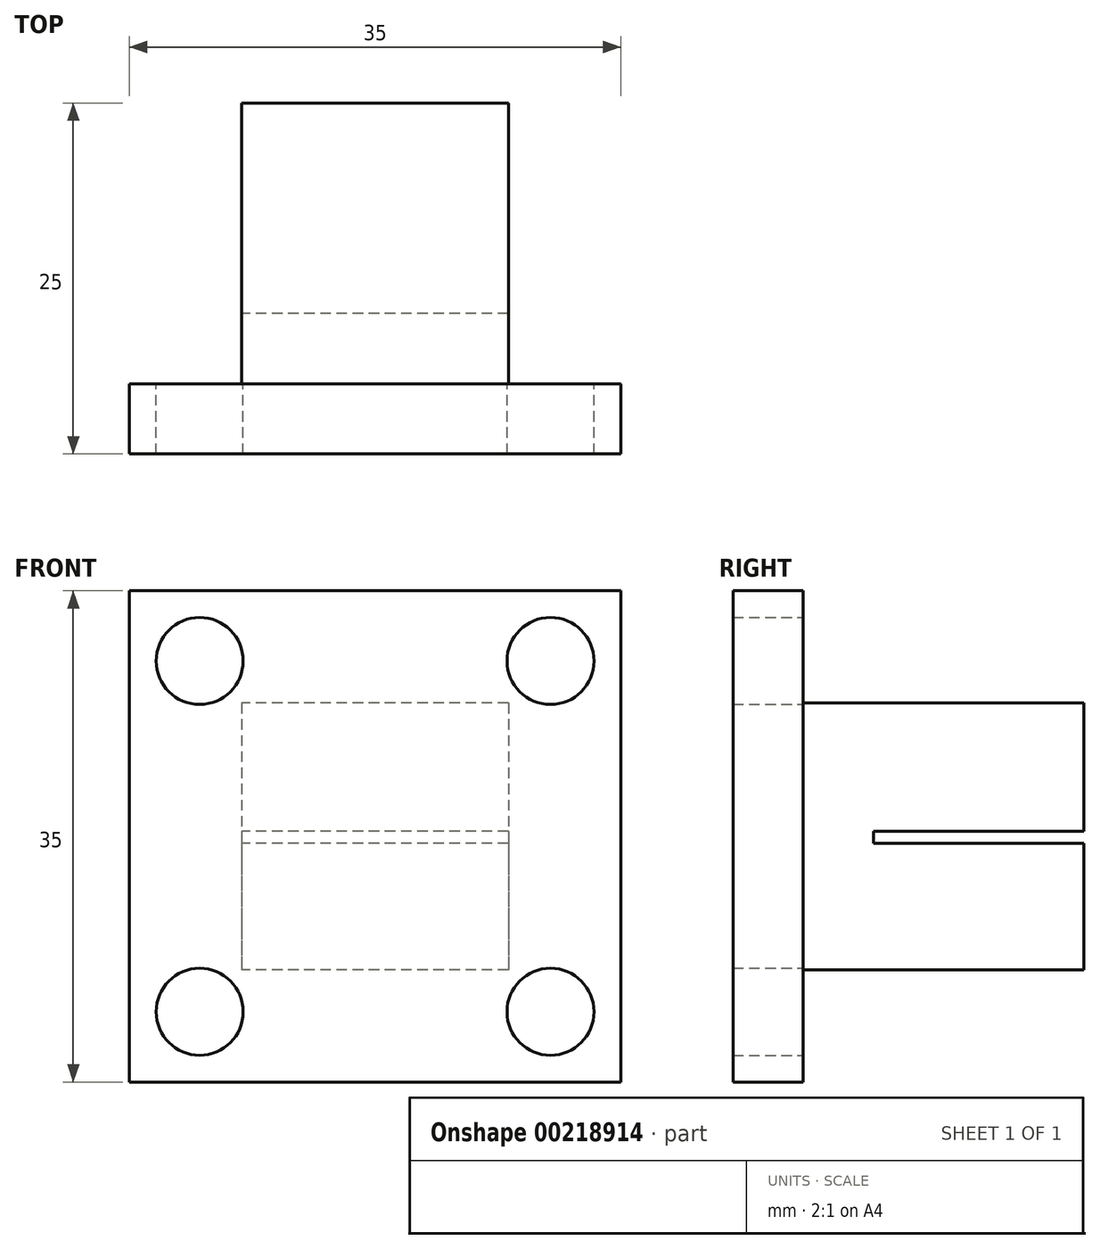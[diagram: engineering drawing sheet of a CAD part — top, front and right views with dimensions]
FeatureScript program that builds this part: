
annotation { "Feature Type Name" : "Feature", "Feature Type Description" : "" }
export const myFeature = defineFeature(function(context is Context, id is Id, definition is map)
    precondition{}
    {
        {
            var Q0;
            Q0=qCreatedBy(makeId("Front.planeOp"),FACE);
            var sketch = newSketch(context, id + "F0", { "sketchPlane" : qUnion([Q0])});
            skLineSegment(sketch, "E0.bottom", {"start": v(-16.94, 0) * mm, "end": v(18.06, 0) * mm});
            skLineSegment(sketch, "E0.top", {"start": v(-16.94, -35) * mm, "end": v(18.06, -35) * mm});
            skLineSegment(sketch, "E0.left", {"start": v(-16.94, 0) * mm, "end": v(-16.94, -35) * mm});
            skLineSegment(sketch, "E0.right", {"start": v(18.06, 0) * mm, "end": v(18.06, -35) * mm});
            skSolve(sketch);
        }
        {
            var Q0;
            Q0 = qSketchRegion(id + "F0", true);
            extrude(context, id + "F1", {"entities" : qUnion([Q0]), "depth" : 5 * mm});
        }
        {
            var Q0;
            Q0=makeQuery(id+"F1.opExtrude","CAP_FACE",FACE,{"disambiguationData":[OSD([sQuery(id+"F0.wireOp",EDGE,"E0.bottom"),sQuery(id+"F0.wireOp",EDGE,"E0.top"),sQuery(id+"F0.wireOp",EDGE,"E0.left"),sQuery(id+"F0.wireOp",EDGE,"E0.right")])],"isStart":true});
            var sketch = newSketch(context, id + "F2", { "sketchPlane" : qUnion([Q0])});
            skCircle(sketch, "E1", {"center": v(-13.06, -5) * mm, "radius": 3.1 * mm});
            skLineSegment(sketch, "E2", {"start": v(-18.06, -17.5) * mm, "end": v(16.94, -17.5) * mm});
            skCircle(sketch, "E3", {"center": v(11.94, -5) * mm, "radius": 3.1 * mm});
            skLineSegment(sketch, "E4", {"start": v(-0.56, -35) * mm, "end": v(-0.56, 0) * mm});
            skCircle(sketch, "E5", {"center": v(-13.06, -30) * mm, "radius": 3.1 * mm});
            skCircle(sketch, "E6", {"center": v(11.94, -30) * mm, "radius": 3.1 * mm});
            skSolve(sketch);
        }
        {
            var Q0;
            Q0 = qSketchRegion(id + "F2", true);
            extrude(context, id + "F3", {"entities" : qUnion([Q0]), "operationType" : NewBodyOperationType.REMOVE, "endBound" : BoundingType.THROUGH_ALL, "oppositeDirection" : true, "depth" : 25 * mm});
        }
        {
            var Q0;
            Q0=makeQuery(id+"F1.opExtrude","CAP_FACE",FACE,{"disambiguationData":[OSD([sQuery(id+"F0.wireOp",EDGE,"E0.bottom"),sQuery(id+"F0.wireOp",EDGE,"E0.top"),sQuery(id+"F0.wireOp",EDGE,"E0.left"),sQuery(id+"F0.wireOp",EDGE,"E0.right")])],"isStart":true});
            var sketch = newSketch(context, id + "F4", { "sketchPlane" : qUnion([Q0])});
            skLineSegment(sketch, "E7.bottom", {"start": v(-10.06, -8) * mm, "end": v(8.94, -8) * mm});
            skLineSegment(sketch, "E7.top", {"start": v(-10.06, -27) * mm, "end": v(8.94, -27) * mm});
            skLineSegment(sketch, "E7.left", {"start": v(-10.06, -8) * mm, "end": v(-10.06, -27) * mm});
            skLineSegment(sketch, "E7.right", {"start": v(8.94, -8) * mm, "end": v(8.94, -27) * mm});
            skSolve(sketch);
        }
        {
            var Q0;
            Q0=makeQuery(id+"F4.imprint","IMPRINT",FACE,{"disambiguationData":[TD([[makeQuery(id+"F4.imprint","IMPRINT",EDGE,{"derivedFrom":sQuery(id+"F4.wireOp",EDGE,"E7.bottom")}),-1.0]])]});
            extrude(context, id + "F5", {"entities" : qUnion([Q0]), "operationType" : NewBodyOperationType.ADD, "depth" : 20 * mm});
        }
        {
            var Q0;
            Q0=makeQuery(id+"F5.opExtrude","CAP_FACE",FACE,{"disambiguationData":[OSD([sQuery(id+"F4.wireOp",EDGE,"E7.bottom"),sQuery(id+"F4.wireOp",EDGE,"E7.top"),sQuery(id+"F4.wireOp",EDGE,"E7.left"),sQuery(id+"F4.wireOp",EDGE,"E7.right")])],"isStart":false});
            var sketch = newSketch(context, id + "F6", { "sketchPlane" : qUnion([Q0])});
            skLineSegment(sketch, "E8.bottom", {"start": v(-10.06, -17.15) * mm, "end": v(8.94, -17.15) * mm});
            skLineSegment(sketch, "E8.top", {"start": v(-10.06, -18) * mm, "end": v(8.94, -18) * mm});
            skLineSegment(sketch, "E8.left", {"start": v(-10.06, -17.15) * mm, "end": v(-10.06, -18) * mm});
            skLineSegment(sketch, "E8.right", {"start": v(8.94, -17.15) * mm, "end": v(8.94, -18) * mm});
            skSolve(sketch);
        }
        {
            var Q0;
            Q0 = qSketchRegion(id + "F6", true);
            extrude(context, id + "F7", {"entities" : qUnion([Q0]), "operationType" : NewBodyOperationType.REMOVE, "oppositeDirection" : true, "depth" : 15 * mm});
        }
    });
